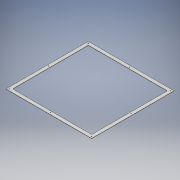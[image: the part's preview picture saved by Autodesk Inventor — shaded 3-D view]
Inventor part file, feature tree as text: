
AUTODESK INVENTOR PART (.ipt)
format: ipt  version: 2019 (Build 230136000, 136)  size: 194,048 bytes
history: native  units: mm
features: other x2, sheet_metal_op x1, sketch x1
ambient origin geometry x8: Origin, YZ Plane, XZ Plane, XY Plane, X Axis, Y Axis, Z Axis, Center Point
bodies: Body1 (feature_tree)
feature tree (4):
  sheet_metal_op  "Face6"
  sketch  "Sketch1"  dims[d0=513.0mm d1=493.0mm d2=10.0mm d3=10.0mm d4=10.0mm d5=110.0mm d6=80.0mm d7=110.0mm d8=110.0mm d9=70.0mm d10=55.0mm d12=0.8mm d13=0.8mm d16=0.8mm d19=0.8mm d20=0.8mm d23=10.0mm d24=10.0mm d25=20.0mm d26=10.0mm d27=2.0mm d28=5.0mm d29=4.2mm d30=10.0mm d31=0.8mm d32=1.5mm]
  other  "Plate6"
  other  "Definition1"
